# Revit family: Gira_128900
name_source: partatom
category: Elektroinstallationen
revit_build: Autodesk Revit 2017 (Build: 20160225_1515(x64)
units: mm (PartAtom-declared; Revit-internal decimal feet)

## family parameters
Basisbauteil = Fläche
Beim Laden mit Abzugskörper schneiden = Nein
Bemaßung runder Anschluss = Durchmesser verwenden
Beschriftungsausrichtung beibehalten = Nein
Gemeinsam genutzt = Nein
Raumberechnungspunkt = Nein
Teiletyp = Normal

## types (1)
- Gira_128900
    BIM = https://media.stage.bim.site 2f.rfa
    Beschreibung = Swit.act.DRA Door,Door communication switching actuator,,DRA,Features:,- Switching actuator for switching light, controlling a door opener on back side doors or other functions via the Gira door communication bus.,- Control of a zero-voltage switching contact 230 V   10 A via the 2-wire bus.,- The switching actuator can be controlled via:,  the buttons Door" and "Light" on the home station,,  the call button on the door station,,  the call button on the home station,,  the buttons of a telephone (in conjunction with DCS-TC gateway).,- The switching actuator can be used in five different operating modes: switching, timer sec., timer min., pulse, and door opener.,- Impulse function for controlling existing automatic staircase mechanisms.,- Binary input for switching functions via a connected mechanical push button.,- Switching time can be adjusted continuously from 1 to 10 s or 1 to 10 min., depending on the function set.,,Notes :,- The switching actuator is intended to be installed in the sub-distribution. If this is not possible, use a common surface-mounted distributor.,- This component enables door communication systems with more than 30 devices to be set up."
    Data sheet = https://katalog.gira.de
    Function = Switch (connect)
    GTIN = 4010337289005
    HAN = 128900
    Hersteller = Gira
    Installation technique = Bus system
    Productwebsite = http://katalog.gira.de
    Typname = DCS swit.act. DRA Door communication
    URL = https://www.gira.de
    Vorgabe-Ansicht = 1219 mm

## geometry (parser evidence)
native form markers: Sweep x2
no freeform markers — native parametric forms only
